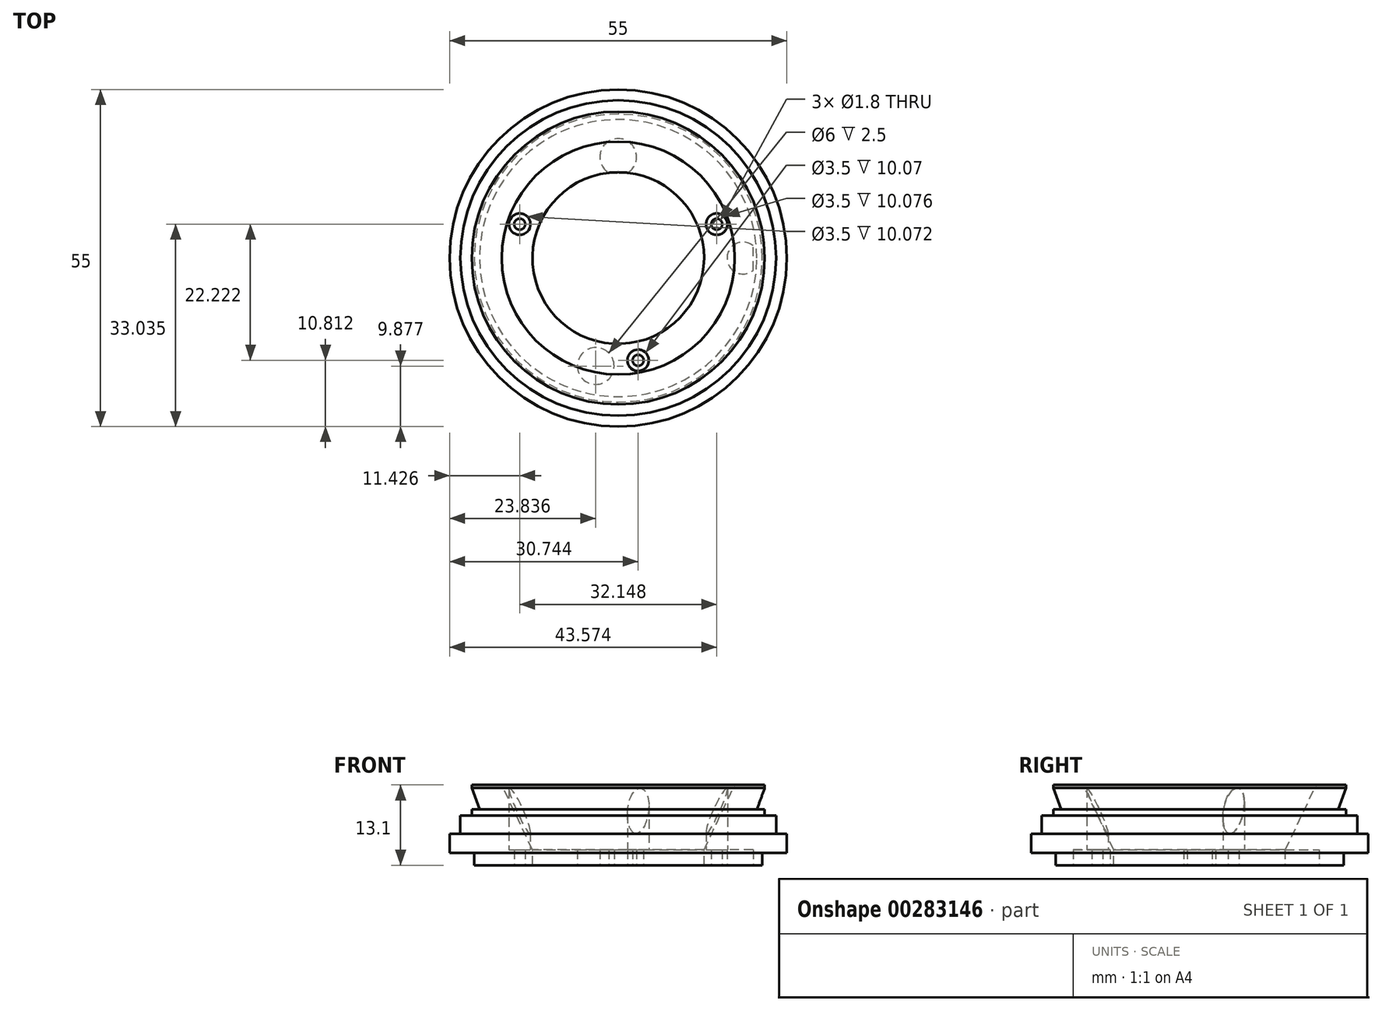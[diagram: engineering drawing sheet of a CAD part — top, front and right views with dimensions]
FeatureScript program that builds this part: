
annotation { "Feature Type Name" : "Feature", "Feature Type Description" : "" }
export const myFeature = defineFeature(function(context is Context, id is Id, definition is map)
    precondition{}
    {
        {
            var Q0;
            Q0=qCreatedBy(makeId("Front.planeOp"),FACE);
            var sketch = newSketch(context, id + "F0", { "sketchPlane" : qUnion([Q0])});
            skLineSegment(sketch, "E0", {"start": v(0, 18.35) * mm, "end": v(0, -26.13) * mm, "construction": true});
            skLineSegment(sketch, "E1", {"start": v(0, 0) * mm, "end": v(34.76, 0) * mm, "construction": true});
            skLineSegment(sketch, "E2", {"start": v(23.5, -35.9) * mm, "end": v(14, -35.9) * mm});
            skLineSegment(sketch, "E3", {"start": v(14, -35.9) * mm, "end": v(14, -33.4) * mm});
            skLineSegment(sketch, "E4", {"start": v(23.9, -22.8) * mm, "end": v(19, -22.8) * mm});
            skLineSegment(sketch, "E5", {"start": v(23.5, -35.9) * mm, "end": v(23.5, -33.9) * mm});
            skLineSegment(sketch, "E6", {"start": v(19, -22.8) * mm, "end": v(14, -33.4) * mm});
            skLineSegment(sketch, "E7", {"start": v(23.9, -22.8) * mm, "end": v(23.9, -23.3) * mm});
            skLineSegment(sketch, "E8", {"start": v(23.9, -23.3) * mm, "end": v(22.63, -26.8) * mm});
            skLineSegment(sketch, "E9", {"start": v(22.63, -26.8) * mm, "end": v(23.9, -26.8) * mm});
            skLineSegment(sketch, "E10", {"start": v(23.9, -26.8) * mm, "end": v(23.9, -27.8) * mm});
            skLineSegment(sketch, "E11", {"start": v(23.9, -27.8) * mm, "end": v(25.75, -27.8) * mm});
            skLineSegment(sketch, "E12", {"start": v(23.5, -33.9) * mm, "end": v(27.5, -33.9) * mm});
            skLineSegment(sketch, "E13", {"start": v(27.5, -33.9) * mm, "end": v(27.5, -30.8) * mm});
            skLineSegment(sketch, "E14", {"start": v(25.75, -27.8) * mm, "end": v(25.75, -30.8) * mm});
            skLineSegment(sketch, "E15", {"start": v(25.75, -30.8) * mm, "end": v(27.5, -30.8) * mm});
            skPoint(sketch, "E16.orphan", {"position": v(27.5, -27.8) * mm});
            skSolve(sketch);
        }
        {
            var Q0;
            Q0=makeQuery(id+"F0.imprint","IMPRINT",FACE,{"disambiguationData":[TD([[makeQuery(id+"F0.imprint","IMPRINT",EDGE,{"derivedFrom":sQuery(id+"F0.wireOp",EDGE,"E2")}),-1.0]])]});
            var Q1;
            Q1=sQuery(id+"F0.wireOp",EDGE,"E0");
            revolve(context, id + "F1", {"entities" : qUnion([Q0]), "axis" : qUnion([Q1]), "revolveType" : RevolveType.FULL});
        }
        {
            var Q0;
            Q0=makeQuery(id+"F1.opRevolve","SWEPT_FACE",FACE,{"disambiguationData":[OSD([sQuery(id+"F0.wireOp",EDGE,"E2")])]});
            var sketch = newSketch(context, id + "F2", { "sketchPlane" : qUnion([Q0])});
            skCircle(sketch, "E17", {"center": v(0, 0) * mm, "radius": 17 * mm, "construction": true});
            skLineSegment(sketch, "E18", {"start": v(0, 0) * mm, "end": v(-19.3, -6.64) * mm, "construction": true});
            skLineSegment(sketch, "E19", {"start": v(0, 0) * mm, "end": v(18.71, -6.44) * mm, "construction": true});
            skLineSegment(sketch, "E20", {"start": v(0, 0) * mm, "end": v(4.4, 22.65) * mm, "construction": true});
            skCircle(sketch, "E21", {"center": v(3.24, 16.69) * mm, "radius": 0.9 * mm});
            skCircle(sketch, "E22", {"center": v(16.07, -5.53) * mm, "radius": 0.9 * mm});
            skCircle(sketch, "E23", {"center": v(-16.07, -5.53) * mm, "radius": 0.9 * mm});
            skSolve(sketch);
        }
        {
            var Q0;
            Q0=qSketchRegion(id+"F2",true);
            extrude(context, id + "F3", {"entities" : qUnion([Q0]), "operationType" : NewBodyOperationType.REMOVE, "oppositeDirection" : true, "depth" : 2.5 * mm});
        }
        {
            var Q0;
            Q0=makeQuery(id+"F1.opRevolve","SWEPT_FACE",FACE,{"disambiguationData":[OSD([sQuery(id+"F0.wireOp",EDGE,"E2")])]});
            var sketch = newSketch(context, id + "F4", { "sketchPlane" : qUnion([Q0])});
            skPoint(sketch, "E24.middle", {"position": v(20.35, 0) * mm});
            skArc(sketch, "E25", {"start": v(22, 2) * mm, "mid": v(17.75, 0) * mm, "end": v(22, -2) * mm});
            skLineSegment(sketch, "E26", {"start": v(22, 2) * mm, "end": v(22, -2) * mm});
            skCircle(sketch, "E27", {"center": v(-3.66, 17.62) * mm, "radius": 3 * mm});
            skCircle(sketch, "E28", {"center": v(0, -16.5) * mm, "radius": 3 * mm});
            skSolve(sketch);
        }
        {
            var Q0;
            Q0=qSketchRegion(id+"F4",true);
            extrude(context, id + "F5", {"entities" : qUnion([Q0]), "operationType" : NewBodyOperationType.REMOVE, "oppositeDirection" : true, "depth" : 2.5 * mm});
        }
        {
            var Q0;
            Q0=makeQuery(id+"F3.boolean.opBoolean","COPY",FACE,{"derivedFrom":makeQuery(id+"F3.opExtrude","CAP_FACE",FACE,{"disambiguationData":[OSD([sQuery(id+"F2.wireOp",EDGE,"E21")])],"isStart":false})});
            var sketch = newSketch(context, id + "F6", { "sketchPlane" : qUnion([Q0])});
            skCircle(sketch, "E29", {"center": v(3.24, 16.69) * mm, "radius": 1.75 * mm});
            skCircle(sketch, "E30.0", {"center": v(-16.07, -5.53) * mm, "radius": 0.9 * mm, "construction": true});
            skCircle(sketch, "E31", {"center": v(-16.07, -5.53) * mm, "radius": 1.75 * mm});
            skCircle(sketch, "E32.0", {"center": v(16.07, -5.53) * mm, "radius": 0.9 * mm, "construction": true});
            skCircle(sketch, "E33", {"center": v(16.07, -5.53) * mm, "radius": 1.75 * mm});
            skSolve(sketch);
        }
        {
            var Q0;
            Q0=qSketchRegion(id+"F6",true);
            extrude(context, id + "F7", {"entities" : qUnion([Q0]), "operationType" : NewBodyOperationType.REMOVE, "endBound" : BoundingType.UP_TO_NEXT, "oppositeDirection" : true, "depth" : 25 * mm});
        }
    });
